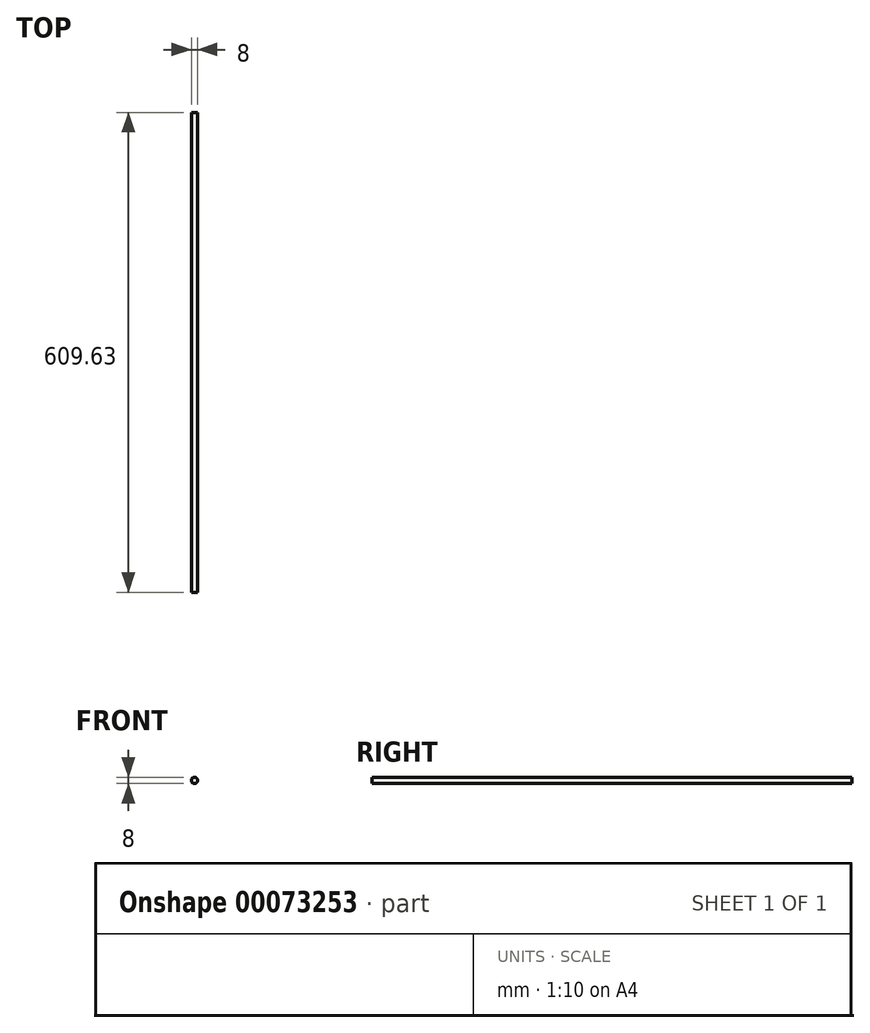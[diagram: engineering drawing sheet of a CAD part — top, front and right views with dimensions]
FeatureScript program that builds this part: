
annotation { "Feature Type Name" : "Feature", "Feature Type Description" : "" }
export const myFeature = defineFeature(function(context is Context, id is Id, definition is map)
    precondition{}
    {
        {
            var Q0;
            Q0=qCreatedBy(makeId("Front.planeOp"),FACE);
            var sketch = newSketch(context, id + "F0", { "sketchPlane" : qUnion([Q0])});
            skCircle(sketch, "E0", {"center": v(0, 0) * mm, "radius": 4 * mm});
            skSolve(sketch);
        }
        {
            var Q0;
            Q0=makeQuery(id+"F0.imprint","IMPRINT",FACE,{"disambiguationData":[TD([[makeQuery(id+"F0.imprint","IMPRINT",EDGE,{"derivedFrom":sQuery(id+"F0.wireOp",EDGE,"E0")}),1.0]])]});
            extrude(context, id + "F1", {"entities" : qUnion([Q0]), "depth" : 863.6 * mm});
        }
        {
            var Q0;
            Q0=makeQuery(id+"F1.opExtrude","CAP_FACE",FACE,{"disambiguationData":[OSD([sQuery(id+"F0.wireOp",EDGE,"E0")])],"isStart":false});
            extrude(context, id + "F2", {"entities" : qUnion([Q0]), "operationType" : NewBodyOperationType.REMOVE, "oppositeDirection" : true, "depth" : 253.97 * mm});
        }
    });
